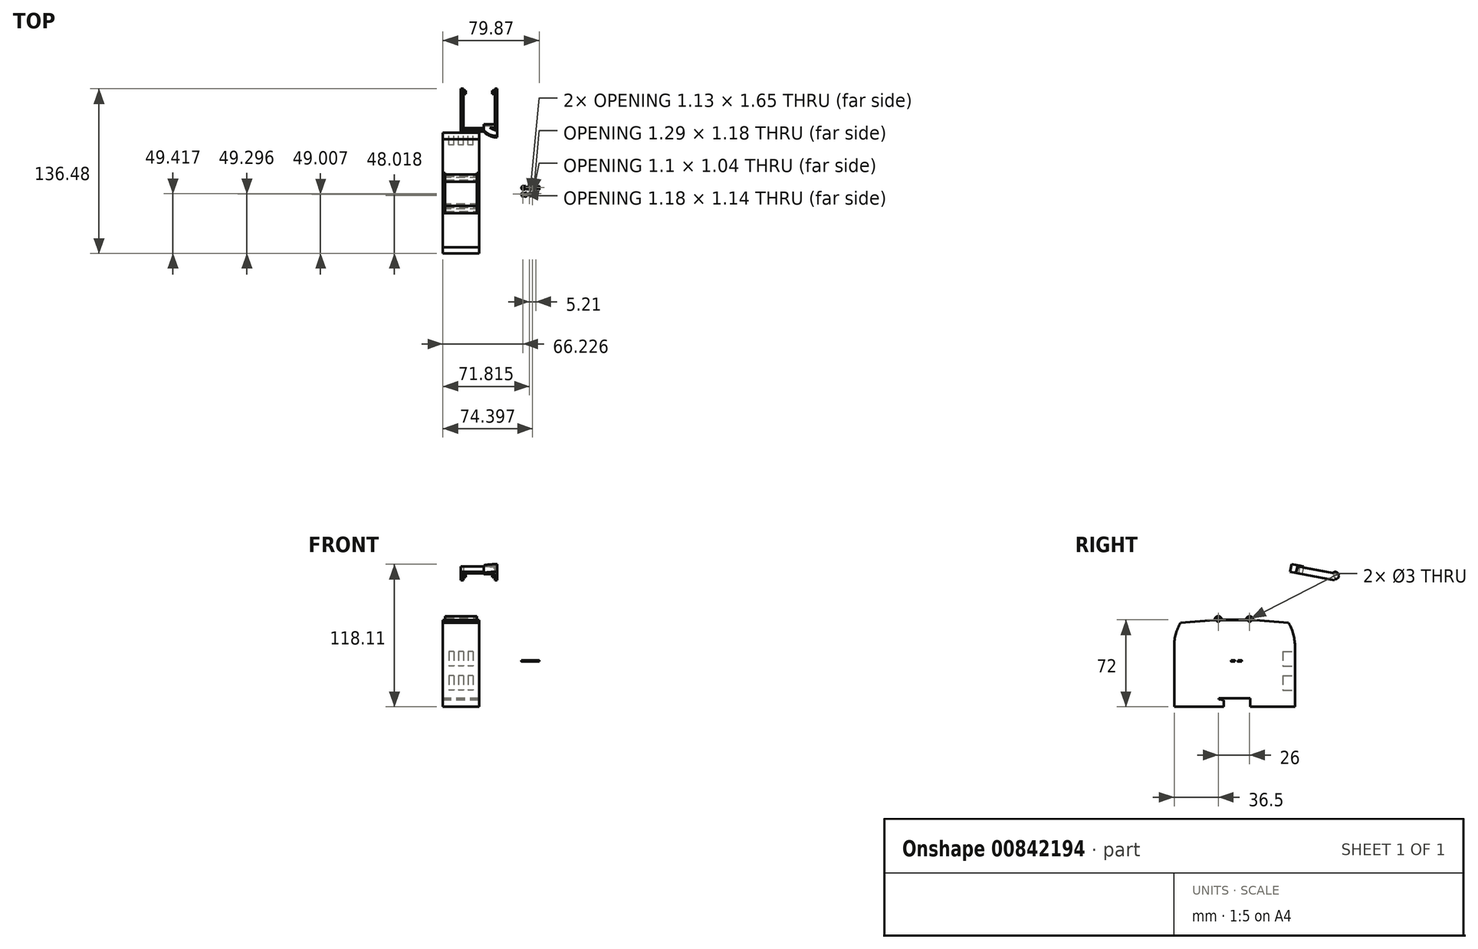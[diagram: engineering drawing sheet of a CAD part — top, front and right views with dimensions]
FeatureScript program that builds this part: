
annotation { "Feature Type Name" : "Feature", "Feature Type Description" : "" }
export const myFeature = defineFeature(function(context is Context, id is Id, definition is map)
    precondition{}
    {
        {
            var Q0;
            Q0=qCreatedBy(makeId("Right.planeOp"),FACE);
            var sketch = newSketch(context, id + "F0", { "sketchPlane" : qUnion([Q0])});
            skLineSegment(sketch, "E0.bottom", {"start": v(50, -37.5) * mm, "end": v(-50, -37.5) * mm});
            skLineSegment(sketch, "E0.top", {"start": v(50, 37.5) * mm, "end": v(-50, 37.5) * mm});
            skLineSegment(sketch, "E0.left", {"start": v(50, -37.5) * mm, "end": v(50, 37.5) * mm});
            skLineSegment(sketch, "E0.right", {"start": v(-50, -37.5) * mm, "end": v(-50, 37.5) * mm});
            skPoint(sketch, "E0.middle", {"position": v(0, 0) * mm});
            skSolve(sketch);
        }
        {
            var Q0;
            Q0=makeQuery(id+"F0.imprint","IMPRINT",FACE,{"disambiguationData":[TD([[makeQuery(id+"F0.imprint","IMPRINT",EDGE,{"derivedFrom":sQuery(id+"F0.wireOp",EDGE,"E0.bottom")}),-1.0]])]});
            extrude(context, id + "F1", {"entities" : qUnion([Q0]), "endBound" : BoundingType.SYMMETRIC, "depth" : 30 * mm, "offsetDistance" : 25 * mm});
        }
        {
            var Q0;
            Q0=makeQuery(id+"F1.opExtrude","CAP_FACE",FACE,{"disambiguationData":[OSD([sQuery(id+"F0.wireOp",EDGE,"E0.bottom"),sQuery(id+"F0.wireOp",EDGE,"E0.top"),sQuery(id+"F0.wireOp",EDGE,"E0.left"),sQuery(id+"F0.wireOp",EDGE,"E0.right")])],"isStart":false});
            var sketch = newSketch(context, id + "F2", { "sketchPlane" : qUnion([Q0])});
            skCircle(sketch, "E1", {"center": v(12.5, 34.5) * mm, "radius": 3 * mm});
            skCircle(sketch, "E2", {"center": v(-13.5, 34.5) * mm, "radius": 3 * mm});
            skLineSegment(sketch, "E3", {"start": v(9.5, 34.5) * mm, "end": v(15.5, 34.5) * mm});
            skLineSegment(sketch, "E4", {"start": v(-10.5, 34.5) * mm, "end": v(-16.5, 34.5) * mm});
            skLineSegment(sketch, "E5", {"start": v(15.5, 34.5) * mm, "end": v(50, 31.5) * mm});
            skLineSegment(sketch, "E6.MirrorCS", {"start": v(-15.5, 34.5) * mm, "end": v(-50, 31.5) * mm});
            skLineSegment(sketch, "E7", {"start": v(-10.5, 34.5) * mm, "end": v(9.5, 34.5) * mm});
            skCircle(sketch, "E8", {"center": v(-13.5, 34.5) * mm, "radius": 1.5 * mm});
            skCircle(sketch, "E9", {"center": v(12.5, 34.5) * mm, "radius": 1.5 * mm});
            skSolve(sketch);
        }
        {
            var Q0;
            {var subQ3=sQuery(id+"F2.wireOp",EDGE,"E2");var subQ8=makeQuery(id+"F2.imprint","INTERSECT",VERTEX,{"disambiguationData":[OD(1.0)],"derivedFrom":[subQ3,sQuery(id+"F2.wireOp",EDGE,"E4")]});Q0=makeQuery(id+"F2.imprint","IMPRINT",FACE,{"disambiguationData":[TD([[makeQuery(id+"F2.imprint","IMPRINT",EDGE,{"disambiguationData":[TD([[subQ8,1.0]])],"derivedFrom":subQ3}),-1.0]])]});}
            var Q1;
            {var subQ0=sQuery(id+"F2.wireOp",EDGE,"E5");Q1=makeQuery(id+"F2.imprint","IMPRINT",FACE,{"disambiguationData":[TD([[makeQuery(id+"F2.imprint","IMPRINT",EDGE,{"derivedFrom":subQ0}),1.0]])]});}
            var Q2;
            {var subQ0=sQuery(id+"F2.wireOp",EDGE,"E7");Q2=makeQuery(id+"F2.imprint","IMPRINT",FACE,{"disambiguationData":[TD([[makeQuery(id+"F2.imprint","IMPRINT",EDGE,{"derivedFrom":subQ0}),1.0]])]});}
            var Q3;
            {var subQ0=sQuery(id+"F2.wireOp",EDGE,"E8");var subQ1=sQuery(id+"F2.wireOp",EDGE,"E4");var subQ2=makeQuery(id+"F2.imprint","INTERSECT",VERTEX,{"disambiguationData":[OD(0.0)],"derivedFrom":[subQ1,subQ0]});Q3=makeQuery(id+"F2.imprint","IMPRINT",FACE,{"disambiguationData":[TD([[makeQuery(id+"F2.imprint","IMPRINT",EDGE,{"disambiguationData":[TD([[subQ2,-1.0]])],"derivedFrom":subQ1}),1.0]])]});}
            var Q4;
            {var subQ0=sQuery(id+"F2.wireOp",EDGE,"E8");var subQ1=sQuery(id+"F2.wireOp",EDGE,"E4");var subQ2=makeQuery(id+"F2.imprint","INTERSECT",VERTEX,{"disambiguationData":[OD(0.0)],"derivedFrom":[subQ1,subQ0]});Q4=makeQuery(id+"F2.imprint","IMPRINT",FACE,{"disambiguationData":[TD([[makeQuery(id+"F2.imprint","IMPRINT",EDGE,{"disambiguationData":[TD([[subQ2,-1.0]])],"derivedFrom":subQ1}),-1.0]])]});}
            var Q5;
            {var subQ0=sQuery(id+"F2.wireOp",EDGE,"E9");var subQ1=sQuery(id+"F2.wireOp",EDGE,"E3");var subQ2=makeQuery(id+"F2.imprint","INTERSECT",VERTEX,{"disambiguationData":[OD(0.0)],"derivedFrom":[subQ1,subQ0]});Q5=makeQuery(id+"F2.imprint","IMPRINT",FACE,{"disambiguationData":[TD([[makeQuery(id+"F2.imprint","IMPRINT",EDGE,{"disambiguationData":[TD([[subQ2,-1.0]])],"derivedFrom":subQ1}),-1.0]])]});}
            var Q6;
            {var subQ0=sQuery(id+"F2.wireOp",EDGE,"E9");var subQ1=sQuery(id+"F2.wireOp",EDGE,"E3");var subQ2=makeQuery(id+"F2.imprint","INTERSECT",VERTEX,{"disambiguationData":[OD(0.0)],"derivedFrom":[subQ1,subQ0]});Q6=makeQuery(id+"F2.imprint","IMPRINT",FACE,{"disambiguationData":[TD([[makeQuery(id+"F2.imprint","IMPRINT",EDGE,{"disambiguationData":[TD([[subQ2,-1.0]])],"derivedFrom":subQ1}),1.0]])]});}
            extrude(context, id + "F3", {"entities" : qUnion([Q0, Q1, Q2, Q3, Q4, Q5, Q6]), "operationType" : NewBodyOperationType.REMOVE, "oppositeDirection" : true, "depth" : 34.2 * mm, "offsetDistance" : 25 * mm});
        }
        {
            var Q0;
            Q0=makeQuery(id+"F1.opExtrude","CAP_FACE",FACE,{"disambiguationData":[OSD([sQuery(id+"F0.wireOp",EDGE,"E0.bottom"),sQuery(id+"F0.wireOp",EDGE,"E0.top"),sQuery(id+"F0.wireOp",EDGE,"E0.left"),sQuery(id+"F0.wireOp",EDGE,"E0.right")])],"isStart":false});
            var sketch = newSketch(context, id + "F4", { "sketchPlane" : qUnion([Q0])});
            skLineSegment(sketch, "E10", {"start": v(50, 31.5) * mm, "end": v(50, -37.5) * mm});
            skLineSegment(sketch, "E11", {"start": v(50, -37.5) * mm, "end": v(-50, -37.5) * mm});
            skLineSegment(sketch, "E12", {"start": v(-50, -37.5) * mm, "end": v(-50, 31.5) * mm});
            skLineSegment(sketch, "E13", {"start": v(-50, 31.5) * mm, "end": v(-16.5, 34.41) * mm});
            skLineSegment(sketch, "E14", {"start": v(15.5, 34.5) * mm, "end": v(50, 31.5) * mm});
            skArc(sketch, "E15", {"start": v(-44.8, 31.95) * mm, "mid": v(-48.7, 22.74) * mm, "end": v(-50, 12.82) * mm});
            skArc(sketch, "E16.MirrorCS", {"start": v(44.8, 31.95) * mm, "mid": v(48.7, 22.74) * mm, "end": v(50, 12.82) * mm});
            skSolve(sketch);
        }
        {
            var Q0;
            {var subQ0=sQuery(id+"F4.wireOp",EDGE,"E14");var subQ1=sQuery(id+"F4.wireOp",EDGE,"E10");var subQ2=makeQuery(id+"F4.imprint","INTERSECT",VERTEX,{"derivedFrom":[subQ1,subQ0]});Q0=makeQuery(id+"F4.imprint","IMPRINT",FACE,{"disambiguationData":[TD([[makeQuery(id+"F4.imprint","IMPRINT",EDGE,{"disambiguationData":[TD([[subQ2,1.0]])],"derivedFrom":subQ1}),1.0]])]});}
            var Q1;
            {var subQ0=sQuery(id+"F4.wireOp",EDGE,"E13");var subQ1=sQuery(id+"F4.wireOp",EDGE,"E12");var subQ2=makeQuery(id+"F4.imprint","INTERSECT",VERTEX,{"derivedFrom":[subQ1,subQ0]});Q1=makeQuery(id+"F4.imprint","IMPRINT",FACE,{"disambiguationData":[TD([[makeQuery(id+"F4.imprint","IMPRINT",EDGE,{"disambiguationData":[TD([[subQ2,1.0]])],"derivedFrom":subQ1}),-1.0]])]});}
            extrude(context, id + "F5", {"entities" : qUnion([Q0, Q1]), "operationType" : NewBodyOperationType.REMOVE, "oppositeDirection" : true, "depth" : 38.1 * mm, "offsetDistance" : 25 * mm});
        }
        {
            var Q0;
            Q0=makeQuery(id+"F1.opExtrude","SWEPT_FACE",FACE,{"disambiguationData":[OSD([sQuery(id+"F0.wireOp",EDGE,"E0.left")])]});
            var sketch = newSketch(context, id + "F6", { "sketchPlane" : qUnion([Q0])});
            skLineSegment(sketch, "E17.bottom", {"start": v(-10, 8.24) * mm, "end": v(-6, 8.24) * mm});
            skLineSegment(sketch, "E17.top", {"start": v(-10, -3.76) * mm, "end": v(-6, -3.76) * mm});
            skLineSegment(sketch, "E17.left", {"start": v(-10, 8.24) * mm, "end": v(-10, -3.76) * mm});
            skLineSegment(sketch, "E17.right", {"start": v(-6, 8.24) * mm, "end": v(-6, -3.76) * mm});
            skLineSegment(sketch, "E18.0.1.0", {"start": v(-6, -11.76) * mm, "end": v(-6, -23.76) * mm});
            skLineSegment(sketch, "E18.0.1.1", {"start": v(-10, -11.76) * mm, "end": v(-6, -11.76) * mm});
            skLineSegment(sketch, "E18.0.1.2", {"start": v(-10, -11.76) * mm, "end": v(-10, -23.76) * mm});
            skLineSegment(sketch, "E18.0.1.3", {"start": v(-10, -23.76) * mm, "end": v(-6, -23.76) * mm});
            skLineSegment(sketch, "E18.1.0.0", {"start": v(2, 8.24) * mm, "end": v(2, -3.76) * mm});
            skLineSegment(sketch, "E18.1.0.1", {"start": v(-2, 8.24) * mm, "end": v(2, 8.24) * mm});
            skLineSegment(sketch, "E18.1.0.2", {"start": v(-2, 8.24) * mm, "end": v(-2, -3.76) * mm});
            skLineSegment(sketch, "E18.1.0.3", {"start": v(-2, -3.76) * mm, "end": v(2, -3.76) * mm});
            skLineSegment(sketch, "E18.1.1.0", {"start": v(2, -11.76) * mm, "end": v(2, -23.76) * mm});
            skLineSegment(sketch, "E18.1.1.1", {"start": v(-2, -11.76) * mm, "end": v(2, -11.76) * mm});
            skLineSegment(sketch, "E18.1.1.2", {"start": v(-2, -11.76) * mm, "end": v(-2, -23.76) * mm});
            skLineSegment(sketch, "E18.1.1.3", {"start": v(-2, -23.76) * mm, "end": v(2, -23.76) * mm});
            skLineSegment(sketch, "E18.2.0.0", {"start": v(10, 8.24) * mm, "end": v(10, -3.76) * mm});
            skLineSegment(sketch, "E18.2.0.1", {"start": v(6, 8.24) * mm, "end": v(10, 8.24) * mm});
            skLineSegment(sketch, "E18.2.0.2", {"start": v(6, 8.24) * mm, "end": v(6, -3.76) * mm});
            skLineSegment(sketch, "E18.2.0.3", {"start": v(6, -3.76) * mm, "end": v(10, -3.76) * mm});
            skLineSegment(sketch, "E18.2.1.0", {"start": v(10, -11.76) * mm, "end": v(10, -23.76) * mm});
            skLineSegment(sketch, "E18.2.1.1", {"start": v(6, -11.76) * mm, "end": v(10, -11.76) * mm});
            skLineSegment(sketch, "E18.2.1.2", {"start": v(6, -11.76) * mm, "end": v(6, -23.76) * mm});
            skLineSegment(sketch, "E18.2.1.3", {"start": v(6, -23.76) * mm, "end": v(10, -23.76) * mm});
            skLineSegment(sketch, "E18.direction1", {"start": v(-6, -3.76) * mm, "end": v(2, -3.76) * mm, "construction": true});
            skLineSegment(sketch, "E18.direction2", {"start": v(-6, -3.76) * mm, "end": v(-6, -23.76) * mm, "construction": true});
            skSolve(sketch);
        }
        {
            var Q0;
            Q0=makeQuery(id+"F6.imprint","IMPRINT",FACE,{"disambiguationData":[TD([[makeQuery(id+"F6.imprint","IMPRINT",EDGE,{"derivedFrom":sQuery(id+"F6.wireOp",EDGE,"E17.bottom")}),-1.0]])]});
            var Q1;
            Q1=makeQuery(id+"F6.imprint","IMPRINT",FACE,{"disambiguationData":[TD([[makeQuery(id+"F6.imprint","IMPRINT",EDGE,{"derivedFrom":sQuery(id+"F6.wireOp",EDGE,"E18.1.0.0")}),-1.0]])]});
            var Q2;
            Q2=makeQuery(id+"F6.imprint","IMPRINT",FACE,{"disambiguationData":[TD([[makeQuery(id+"F6.imprint","IMPRINT",EDGE,{"derivedFrom":sQuery(id+"F6.wireOp",EDGE,"E18.2.0.0")}),-1.0]])]});
            var Q3;
            Q3=makeQuery(id+"F6.imprint","IMPRINT",FACE,{"disambiguationData":[TD([[makeQuery(id+"F6.imprint","IMPRINT",EDGE,{"derivedFrom":sQuery(id+"F6.wireOp",EDGE,"E18.1.1.0")}),-1.0]])]});
            var Q4;
            Q4=makeQuery(id+"F6.imprint","IMPRINT",FACE,{"disambiguationData":[TD([[makeQuery(id+"F6.imprint","IMPRINT",EDGE,{"derivedFrom":sQuery(id+"F6.wireOp",EDGE,"E18.0.1.0")}),-1.0]])]});
            var Q5;
            Q5=makeQuery(id+"F6.imprint","IMPRINT",FACE,{"disambiguationData":[TD([[makeQuery(id+"F6.imprint","IMPRINT",EDGE,{"derivedFrom":sQuery(id+"F6.wireOp",EDGE,"E18.2.1.0")}),-1.0]])]});
            extrude(context, id + "F7", {"entities" : qUnion([Q0, Q1, Q2, Q3, Q4, Q5]), "operationType" : NewBodyOperationType.REMOVE, "oppositeDirection" : true, "depth" : 10 * mm, "offsetDistance" : 25 * mm});
        }
        {
            var Q0;
            Q0=qCreatedBy(makeId("Right.planeOp"),FACE);
            var sketch = newSketch(context, id + "F8", { "sketchPlane" : qUnion([Q0])});
            skLineSegment(sketch, "E19", {"start": v(52.54, 78.64) * mm, "end": v(81.27, 73.22) * mm});
            skLineSegment(sketch, "E20", {"start": v(51.2, 74.36) * mm, "end": v(52.54, 78.64) * mm});
            skCircle(sketch, "E21", {"center": v(83.48, 71.24) * mm, "radius": 3 * mm});
            skLineSegment(sketch, "E22", {"start": v(82.92, 68.3) * mm, "end": v(51.2, 74.36) * mm});
            skSolve(sketch);
        }
        {
            var Q0;
            {var subQ0=sQuery(id+"F8.wireOp",EDGE,"E19");Q0=makeQuery(id+"F8.imprint","IMPRINT",FACE,{"disambiguationData":[TD([[makeQuery(id+"F8.imprint","IMPRINT",EDGE,{"derivedFrom":subQ0}),-1.0]])]});}
            var Q1;
            {var subQ0=sQuery(id+"F8.wireOp",EDGE,"c0bd57a7-42e3-4fa6-87de-41fbec08b3d9");Q1=makeQuery(id+"F8.imprint","IMPRINT",FACE,{"disambiguationData":[TD([[makeQuery(id+"F8.imprint","IMPRINT",EDGE,{"derivedFrom":subQ0}),1.0]])]});}
            var Q2;
            {var subQ0=sQuery(id+"F8.wireOp",EDGE,"c0bd57a7-42e3-4fa6-87de-41fbec08b3d9");Q2=makeQuery(id+"F8.imprint","IMPRINT",FACE,{"disambiguationData":[TD([[makeQuery(id+"F8.imprint","IMPRINT",EDGE,{"derivedFrom":subQ0}),-1.0]])]});}
            var Q3;
            {var subQ0=sQuery(id+"F8.wireOp",EDGE,"E21");var subQ1=makeQuery(id+"F8.imprint","INTERSECT",VERTEX,{"derivedFrom":[subQ0,sQuery(id+"F8.wireOp",EDGE,"E22")]});Q3=makeQuery(id+"F8.imprint","IMPRINT",FACE,{"disambiguationData":[TD([[makeQuery(id+"F8.imprint","IMPRINT",EDGE,{"disambiguationData":[TD([[subQ1,1.0]])],"derivedFrom":subQ0}),1.0]])]});}
            extrude(context, id + "F9", {"entities" : qUnion([Q0, Q1, Q2, Q3]), "depth" : 30 * mm, "offsetDistance" : 25 * mm});
        }
        {
            var Q0;
            Q0=makeQuery(id+"F9.opExtrude","SWEPT_FACE",FACE,{"disambiguationData":[OSD([sQuery(id+"F8.wireOp",EDGE,"E22")])]});
            var sketch = newSketch(context, id + "F10", { "sketchPlane" : qUnion([Q0])});
            skLineSegment(sketch, "E23", {"start": v(30, -36.31) * mm, "end": v(0, -36.31) * mm});
            skLineSegment(sketch, "E24", {"start": v(0, -36.31) * mm, "end": v(0, -73.31) * mm});
            skLineSegment(sketch, "E25", {"start": v(0, -73.31) * mm, "end": v(2, -73.31) * mm});
            skLineSegment(sketch, "E26", {"start": v(2, -73.31) * mm, "end": v(2, -38.31) * mm});
            skLineSegment(sketch, "E27", {"start": v(2, -38.31) * mm, "end": v(28, -38.31) * mm});
            skLineSegment(sketch, "E28", {"start": v(28, -38.31) * mm, "end": v(28, -73.31) * mm});
            skLineSegment(sketch, "E29", {"start": v(28, -73.31) * mm, "end": v(30, -73.31) * mm});
            skLineSegment(sketch, "E30", {"start": v(30, -73.31) * mm, "end": v(30, -36.31) * mm});
            skLineSegment(sketch, "E31", {"start": v(28, -73.31) * mm, "end": v(1, -73.31) * mm});
            skSolve(sketch);
        }
        {
            var Q0;
            {var subQ0=sQuery(id+"F10.wireOp",EDGE,"E27");Q0=makeQuery(id+"F10.imprint","IMPRINT",FACE,{"disambiguationData":[TD([[makeQuery(id+"F10.imprint","IMPRINT",EDGE,{"derivedFrom":subQ0}),-1.0]])]});}
            var Q1;
            {var subQ0=sQuery(id+"F10.wireOp",EDGE,"E31");var subQ1=sQuery(id+"F10.wireOp",EDGE,"E26");var subQ2=makeQuery(id+"F10.imprint","INTERSECT",VERTEX,{"derivedFrom":[subQ1,subQ0]});Q1=makeQuery(id+"F10.imprint","IMPRINT",FACE,{"disambiguationData":[TD([[makeQuery(id+"F10.imprint","IMPRINT",EDGE,{"disambiguationData":[TD([[subQ2,-1.0]])],"derivedFrom":subQ1}),-1.0]])]});}
            extrude(context, id + "F11", {"entities" : qUnion([Q0, Q1]), "operationType" : NewBodyOperationType.REMOVE, "oppositeDirection" : true, "depth" : 25 * mm, "offsetDistance" : 25 * mm});
        }
        {
            var Q0;
            Q0=makeQuery(id+"F11.boolean.opBoolean","COPY",FACE,{"derivedFrom":makeQuery(id+"F11.opExtrude","SWEPT_FACE",FACE,{"disambiguationData":[OSD([sQuery(id+"F10.wireOp",EDGE,"E26")])]})});
            var sketch = newSketch(context, id + "F12", { "sketchPlane" : qUnion([Q0])});
            skCircle(sketch, "E32", {"center": v(83.48, 71.24) * mm, "radius": 1.5 * mm});
            skSolve(sketch);
        }
        {
            var Q0;
            Q0=makeQuery(id+"F12.imprint","IMPRINT",FACE,{"disambiguationData":[TD([[makeQuery(id+"F12.imprint","IMPRINT",EDGE,{"derivedFrom":sQuery(id+"F12.wireOp",EDGE,"E32")}),1.0]])]});
            extrude(context, id + "F13", {"entities" : qUnion([Q0]), "operationType" : NewBodyOperationType.ADD, "depth" : 2 * mm, "offsetDistance" : 25 * mm});
        }
        {
            var Q0;
            Q0=makeQuery(id+"F11.boolean.opBoolean","COPY",FACE,{"derivedFrom":makeQuery(id+"F11.opExtrude","SWEPT_FACE",FACE,{"disambiguationData":[OSD([sQuery(id+"F10.wireOp",EDGE,"E28")])]})});
            var sketch = newSketch(context, id + "F14", { "sketchPlane" : qUnion([Q0])});
            skCircle(sketch, "E33", {"center": v(-83.48, 71.24) * mm, "radius": 1.5 * mm});
            skSolve(sketch);
        }
        {
            var Q0;
            Q0=makeQuery(id+"F14.imprint","IMPRINT",FACE,{"disambiguationData":[TD([[makeQuery(id+"F14.imprint","IMPRINT",EDGE,{"derivedFrom":sQuery(id+"F14.wireOp",EDGE,"E33")}),1.0]])]});
            extrude(context, id + "F15", {"entities" : qUnion([Q0]), "operationType" : NewBodyOperationType.ADD, "depth" : 2 * mm, "offsetDistance" : 25 * mm});
        }
        {
            var Q0;
            Q0=makeQuery(id+"F9.opExtrude","SWEPT_FACE",FACE,{"disambiguationData":[OSD([sQuery(id+"F8.wireOp",EDGE,"E22")])]});
            var sketch = newSketch(context, id + "F16", { "sketchPlane" : qUnion([Q0])});
            skLineSegment(sketch, "E34", {"start": v(30, -36.31) * mm, "end": v(30, -68.6) * mm});
            skLineSegment(sketch, "E35", {"start": v(30, -68.6) * mm, "end": v(0, -68.6) * mm});
            skLineSegment(sketch, "E36", {"start": v(0, -68.6) * mm, "end": v(0, -36.31) * mm});
            skLineSegment(sketch, "E37", {"start": v(0, -36.31) * mm, "end": v(30, -36.31) * mm});
            skSolve(sketch);
        }
        {
            var Q0;
            {var subQ1=makeQuery(id+"F11.boolean.opBoolean","COPY",EDGE,{"derivedFrom":makeQuery(id+"F11.opExtrude","CAP_EDGE",EDGE,{"disambiguationData":[OSD([sQuery(id+"F10.wireOp",EDGE,"E26")])],"isStart":true})});Q0=makeQuery(id+"F16.imprint","IMPRINT",FACE,{"disambiguationData":[TD([[makeQuery(id+"F16.imprint","IMPRINT",EDGE,{"derivedFrom":subQ1}),-1.0]])]});}
            var Q1;
            {var subQ3=sQuery(id+"F16.wireOp",EDGE,"E34");Q1=makeQuery(id+"F16.imprint","IMPRINT",FACE,{"disambiguationData":[TD([[makeQuery(id+"F16.imprint","IMPRINT",EDGE,{"derivedFrom":subQ3}),1.0]])]});}
            extrude(context, id + "F17", {"entities" : qUnion([Q0, Q1]), "operationType" : NewBodyOperationType.ADD, "depth" : 1 * mm, "offsetDistance" : 25 * mm});
        }
        {
            var Q0;
            Q0=makeQuery(id+"F17.opExtrude","CAP_FACE",FACE,{"disambiguationData":[OSD([sQuery(id+"F16.wireOp",EDGE,"E34"),sQuery(id+"F16.wireOp",EDGE,"E35"),sQuery(id+"F16.wireOp",EDGE,"E36"),sQuery(id+"F16.wireOp",EDGE,"E37")])],"isStart":false});
            var sketch = newSketch(context, id + "F18", { "sketchPlane" : qUnion([Q0])});
            skLineSegment(sketch, "E38", {"start": v(0, -41.31) * mm, "end": v(21.34, -41.31) * mm});
            skArc(sketch, "E39", {"start": v(30, -36.31) * mm, "mid": v(25, -37.65) * mm, "end": v(21.34, -41.31) * mm});
            skLineSegment(sketch, "E40.0", {"start": v(0.38, -36.31) * mm, "end": v(18.82, -36.31) * mm});
            skArc(sketch, "E40.1", {"start": v(30, -31.31) * mm, "mid": v(23.88, -32.62) * mm, "end": v(18.82, -36.31) * mm});
            skLineSegment(sketch, "E41", {"start": v(30, -31.31) * mm, "end": v(30, -36.31) * mm});
            skLineSegment(sketch, "E42", {"start": v(30, -36.31) * mm, "end": v(18.82, -36.31) * mm});
            skLineSegment(sketch, "E43", {"start": v(18.82, -36.31) * mm, "end": v(18.82, -41.31) * mm});
            skLineSegment(sketch, "E44", {"start": v(18.82, -41.31) * mm, "end": v(30, -41.31) * mm});
            skSolve(sketch);
        }
        {
            var Q0;
            Q0=makeQuery(id+"F18.imprint","IMPRINT",FACE,{"disambiguationData":[TD([[makeQuery(id+"F18.imprint","IMPRINT",EDGE,{"derivedFrom":sQuery(id+"F18.wireOp",EDGE,"E40.1")}),1.0]])]});
            var Q1;
            {var subQ0=sQuery(id+"F18.wireOp",EDGE,"E39");Q1=makeQuery(id+"F18.imprint","IMPRINT",FACE,{"disambiguationData":[TD([[makeQuery(id+"F18.imprint","IMPRINT",EDGE,{"derivedFrom":subQ0}),1.0]])]});}
            var Q2;
            {var subQ0=sQuery(id+"F18.wireOp",EDGE,"E39");Q2=makeQuery(id+"F18.imprint","IMPRINT",FACE,{"disambiguationData":[TD([[makeQuery(id+"F18.imprint","IMPRINT",EDGE,{"derivedFrom":subQ0}),-1.0]])]});}
            extrude(context, id + "F19", {"entities" : qUnion([Q0, Q1, Q2]), "operationType" : NewBodyOperationType.ADD, "oppositeDirection" : true, "depth" : 6.4 * mm, "offsetDistance" : 25 * mm});
        }
        {
            var Q0;
            Q0=qCreatedBy(makeId("Top.planeOp"),FACE);
            var sketch = newSketch(context, id + "F20", { "sketchPlane" : qUnion([Q0])});
            skText(sketch, "E45", { "text": "CM1241\nRS 485", "fontName": "OpenSans-Regular.ttf"});
            const initialGuessF20  = {"E45": [0.04988, 0.00286, 1, 0, 0.003]};
            skSetInitialGuess(sketch, initialGuessF20);
            skSolve(sketch);
        }
        {
            var Q0;
            Q0 = qSketchRegion(id + "F20", true);
            extrude(context, id + "F21", {"entities" : qUnion([Q0]), "operationType" : NewBodyOperationType.ADD, "depth" : 1 * mm, "offsetDistance" : 25 * mm});
        }
        {
            var Q0;
            Q0=makeQuery(id+"F1.opExtrude","SWEPT_FACE",FACE,{"disambiguationData":[OSD([sQuery(id+"F0.wireOp",EDGE,"E0.right")])]});
            var sketch = newSketch(context, id + "F22", { "sketchPlane" : qUnion([Q0])});
            skLineSegment(sketch, "E46", {"start": v(-15.04, 34.4) * mm, "end": v(-13.04, 34.4) * mm});
            skLineSegment(sketch, "E47", {"start": v(-13.04, 34.4) * mm, "end": v(-13.04, 39.05) * mm});
            skLineSegment(sketch, "E48", {"start": v(-13.04, 39.05) * mm, "end": v(-15.27, 39.05) * mm});
            skLineSegment(sketch, "E49", {"start": v(-15.27, 39.05) * mm, "end": v(-15.04, 34.4) * mm});
            skLineSegment(sketch, "E50.MirrorCS", {"start": v(13.04, 34.4) * mm, "end": v(13.04, 39.05) * mm});
            skLineSegment(sketch, "E51.MirrorCS", {"start": v(13.04, 39.05) * mm, "end": v(15.27, 39.05) * mm});
            skLineSegment(sketch, "E52.MirrorCS", {"start": v(15.27, 39.05) * mm, "end": v(15.04, 34.4) * mm});
            skLineSegment(sketch, "E53.MirrorCS", {"start": v(15.04, 34.4) * mm, "end": v(13.04, 34.4) * mm});
            skSolve(sketch);
        }
        {
            var Q0;
            Q0=makeQuery(id+"F22.imprint","IMPRINT",FACE,{"disambiguationData":[TD([[makeQuery(id+"F22.imprint","IMPRINT",EDGE,{"derivedFrom":sQuery(id+"F22.wireOp",EDGE,"E46")}),1.0]])]});
            var Q1;
            Q1=makeQuery(id+"F22.imprint","IMPRINT",FACE,{"disambiguationData":[TD([[makeQuery(id+"F22.imprint","IMPRINT",EDGE,{"derivedFrom":sQuery(id+"F22.wireOp",EDGE,"E50.MirrorCS")}),-1.0]])]});
            extrude(context, id + "F23", {"entities" : qUnion([Q0, Q1]), "operationType" : NewBodyOperationType.REMOVE, "oppositeDirection" : true, "depth" : 97.5 * mm, "offsetDistance" : 25 * mm});
        }
        {
            var Q0;
            Q0=makeQuery(id+"F1.opExtrude","CAP_FACE",FACE,{"disambiguationData":[OSD([sQuery(id+"F0.wireOp",EDGE,"E0.bottom"),sQuery(id+"F0.wireOp",EDGE,"E0.top"),sQuery(id+"F0.wireOp",EDGE,"E0.left"),sQuery(id+"F0.wireOp",EDGE,"E0.right")])],"isStart":true});
            var sketch = newSketch(context, id + "F24", { "sketchPlane" : qUnion([Q0])});
            skLineSegment(sketch, "E54", {"start": v(0, -30.5) * mm, "end": v(-13, -30.5) * mm});
            skLineSegment(sketch, "E55", {"start": v(-13, -30.5) * mm, "end": v(13, -30.5) * mm});
            skLineSegment(sketch, "E56", {"start": v(13, -30.5) * mm, "end": v(13, -37.5) * mm});
            skLineSegment(sketch, "E57", {"start": v(-13, -30.5) * mm, "end": v(-13, -37.5) * mm});
            skLineSegment(sketch, "E58", {"start": v(13, -30.5) * mm, "end": v(13, -31.5) * mm});
            skLineSegment(sketch, "E59", {"start": v(13, -31.5) * mm, "end": v(9, -32) * mm});
            skLineSegment(sketch, "E60", {"start": v(9, -32) * mm, "end": v(9, -37.5) * mm});
            skSolve(sketch);
        }
        {
            var Q0;
            {var subQ1=sQuery(id+"F24.wireOp",EDGE,"E57");Q0=makeQuery(id+"F24.imprint","IMPRINT",FACE,{"disambiguationData":[TD([[makeQuery(id+"F24.imprint","IMPRINT",EDGE,{"derivedFrom":subQ1}),1.0]])]});}
            extrude(context, id + "F25", {"entities" : qUnion([Q0]), "operationType" : NewBodyOperationType.REMOVE, "oppositeDirection" : true, "depth" : 45 * mm, "offsetDistance" : 25 * mm});
        }
    });
